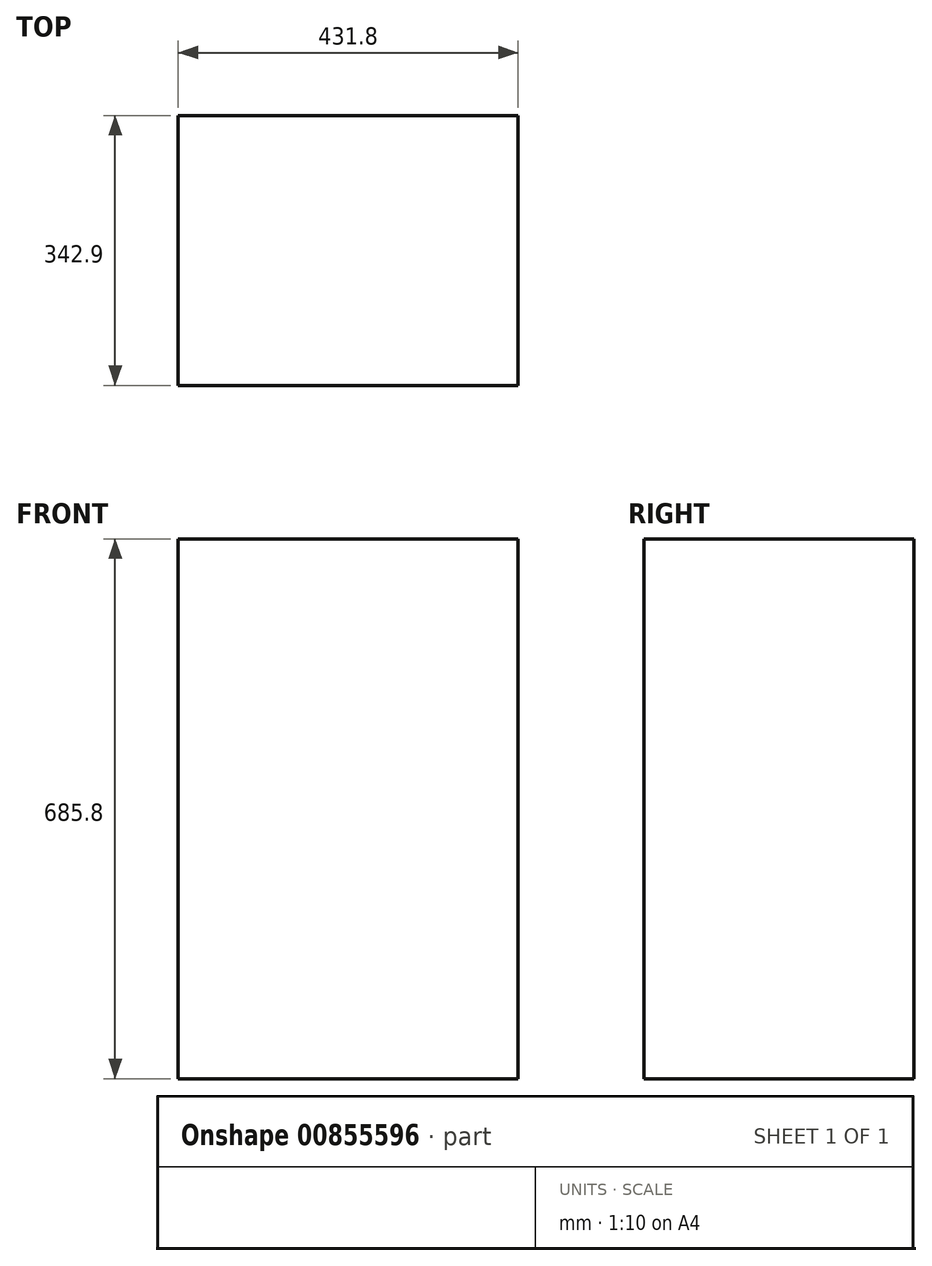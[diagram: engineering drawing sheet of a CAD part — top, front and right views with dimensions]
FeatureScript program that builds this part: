
annotation { "Feature Type Name" : "Feature", "Feature Type Description" : "" }
export const myFeature = defineFeature(function(context is Context, id is Id, definition is map)
    precondition{}
    {
        {
            var Q0;
            Q0=qCreatedBy(makeId("Top.planeOp"),FACE);
            var sketch = newSketch(context, id + "F0", { "sketchPlane" : qUnion([Q0])});
            skLineSegment(sketch, "E0.bottom", {"start": v(0, 0) * mm, "end": v(431.8, 0) * mm});
            skLineSegment(sketch, "E0.top", {"start": v(0, 342.9) * mm, "end": v(431.8, 342.9) * mm});
            skLineSegment(sketch, "E0.left", {"start": v(0, 0) * mm, "end": v(0, 342.9) * mm});
            skLineSegment(sketch, "E0.right", {"start": v(431.8, 0) * mm, "end": v(431.8, 342.9) * mm});
            skSolve(sketch);
        }
        {
            var Q0;
            Q0 = qSketchRegion(id + "F0", true);
            extrude(context, id + "F1", {"entities" : qUnion([Q0]), "depth" : 685.8 * mm, "offsetDistance" : 25.4 * mm});
        }
    });
